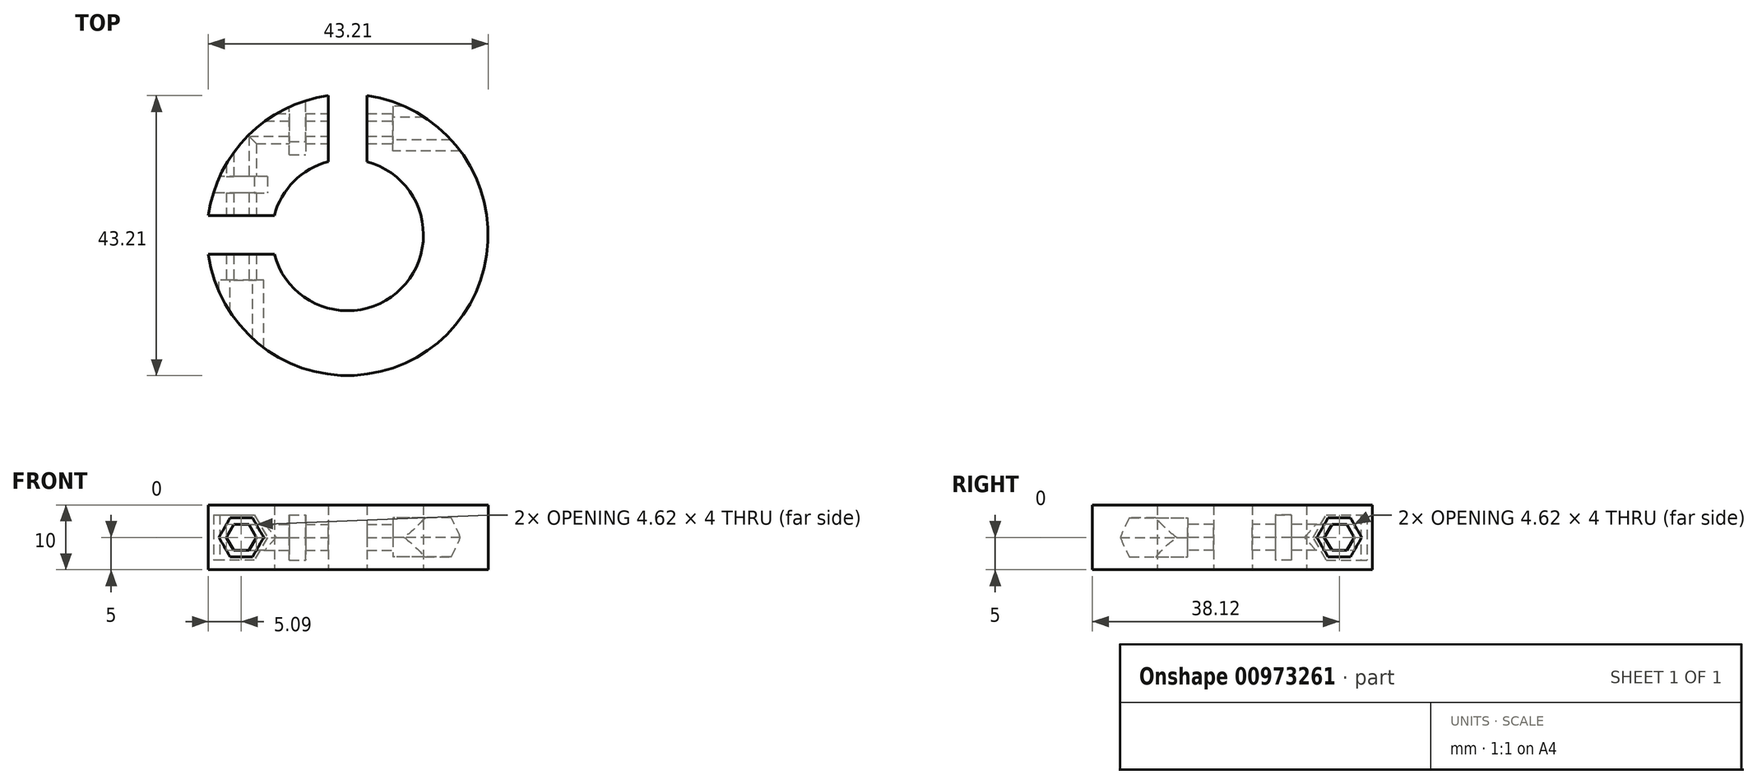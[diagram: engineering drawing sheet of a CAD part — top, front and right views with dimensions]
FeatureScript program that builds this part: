
annotation { "Feature Type Name" : "Feature", "Feature Type Description" : "" }
export const myFeature = defineFeature(function(context is Context, id is Id, definition is map)
    precondition{}
    {
        {
            var Q0;
            Q0=qCreatedBy(makeId("Top.planeOp"),FACE);
            var sketch = newSketch(context, id + "F0", { "sketchPlane" : qUnion([Q0])});
            skCircle(sketch, "E0", {"center": v(0, 0) * mm, "radius": 11.71 * mm});
            skCircle(sketch, "E1", {"center": v(0, 0) * mm, "radius": 21.71 * mm});
            skLineSegment(sketch, "E2.bottom", {"start": v(3, 6.36) * mm, "end": v(-3, 6.36) * mm});
            skLineSegment(sketch, "E2.top", {"start": v(3, 26.36) * mm, "end": v(-3, 26.36) * mm});
            skLineSegment(sketch, "E2.left", {"start": v(3, 6.36) * mm, "end": v(3, 26.36) * mm});
            skLineSegment(sketch, "E2.right", {"start": v(-3, 6.36) * mm, "end": v(-3, 26.36) * mm});
            skPoint(sketch, "E2.middle", {"position": v(0, 16.36) * mm});
            skLineSegment(sketch, "E3.bottom", {"start": v(-26.5, 3) * mm, "end": v(-6.5, 3) * mm});
            skLineSegment(sketch, "E3.top", {"start": v(-26.5, -3) * mm, "end": v(-6.5, -3) * mm});
            skLineSegment(sketch, "E3.left", {"start": v(-26.5, 3) * mm, "end": v(-26.5, -3) * mm});
            skLineSegment(sketch, "E3.right", {"start": v(-6.5, 3) * mm, "end": v(-6.5, -3) * mm});
            skPoint(sketch, "E3.middle", {"position": v(-16.5, 0) * mm});
            skSolve(sketch);
        }
        {
            var Q0;
            {var subQ0=sQuery(id+"F0.wireOp",EDGE,"E2.right");var subQ1=sQuery(id+"F0.wireOp",EDGE,"E0");var subQ2=makeQuery(id+"F0.imprint","INTERSECT",VERTEX,{"derivedFrom":[subQ1,subQ0]});Q0=makeQuery(id+"F0.imprint","IMPRINT",FACE,{"disambiguationData":[TD([[makeQuery(id+"F0.imprint","IMPRINT",EDGE,{"disambiguationData":[TD([[subQ2,-1.0]])],"derivedFrom":subQ1}),-1.0]])]});}
            var Q1;
            {var subQ0=sQuery(id+"F0.wireOp",EDGE,"E2.left");var subQ1=sQuery(id+"F0.wireOp",EDGE,"E0");var subQ2=makeQuery(id+"F0.imprint","INTERSECT",VERTEX,{"derivedFrom":[subQ1,subQ0]});Q1=makeQuery(id+"F0.imprint","IMPRINT",FACE,{"disambiguationData":[TD([[makeQuery(id+"F0.imprint","IMPRINT",EDGE,{"disambiguationData":[TD([[subQ2,1.0]])],"derivedFrom":subQ1}),-1.0]])]});}
            extrude(context, id + "F1", {"entities" : qUnion([Q0, Q1]), "depth" : 10 * mm, "offsetDistance" : 25 * mm});
        }
        {
            var Q0;
            Q0=makeQuery(id+"F1.opExtrude","SWEPT_FACE",FACE,{"disambiguationData":[OSD([sQuery(id+"F0.wireOp",EDGE,"E3.bottom")])]});
            var sketch = newSketch(context, id + "F2", { "sketchPlane" : qUnion([Q0])});
            skCircle(sketch, "E4", {"center": v(-16.41, 5) * mm, "radius": 2 * mm});
            skPoint(sketch, "E4.centerSnap0", {"position": v(-11.32, 5) * mm});
            skPoint(sketch, "E4.centerSnap1", {"position": v(-16.41, 10) * mm});
            skCircle(sketch, "E5", {"center": v(-16.41, 5) * mm, "radius": 3 * mm});
            skCircle(sketch, "E6.cCircle", {"center": v(-16.41, 5) * mm, "radius": 2 * mm, "construction": true});
            skLineSegment(sketch, "E6.0", {"start": v(-15.26, 3) * mm, "end": v(-17.57, 3) * mm});
            skLineSegment(sketch, "E6.1", {"start": v(-17.57, 3) * mm, "end": v(-18.72, 5) * mm});
            skLineSegment(sketch, "E6.2", {"start": v(-18.72, 5) * mm, "end": v(-17.57, 7) * mm});
            skLineSegment(sketch, "E6.3", {"start": v(-17.57, 7) * mm, "end": v(-15.26, 7) * mm});
            skLineSegment(sketch, "E6.4", {"start": v(-15.26, 7) * mm, "end": v(-14.1, 5) * mm});
            skLineSegment(sketch, "E6.5", {"start": v(-14.1, 5) * mm, "end": v(-15.26, 3) * mm});
            skPoint(sketch, "E6.0.midPoint", {"position": v(-16.41, 3) * mm});
            skCircle(sketch, "E7.cCircle", {"center": v(-16.41, 5) * mm, "radius": 3 * mm, "construction": true});
            skLineSegment(sketch, "E7.0", {"start": v(-14.68, 2) * mm, "end": v(-18.14, 2) * mm});
            skLineSegment(sketch, "E7.1", {"start": v(-18.14, 2) * mm, "end": v(-19.87, 5) * mm});
            skLineSegment(sketch, "E7.2", {"start": v(-19.87, 5) * mm, "end": v(-18.14, 8) * mm});
            skLineSegment(sketch, "E7.3", {"start": v(-18.14, 8) * mm, "end": v(-14.68, 8) * mm});
            skLineSegment(sketch, "E7.4", {"start": v(-14.68, 8) * mm, "end": v(-12.95, 5) * mm});
            skLineSegment(sketch, "E7.5", {"start": v(-12.95, 5) * mm, "end": v(-14.68, 2) * mm});
            skPoint(sketch, "E7.0.midPoint", {"position": v(-16.41, 2) * mm});
            skCircle(sketch, "E8.cCircle", {"center": v(-16.41, 5) * mm, "radius": 3.5 * mm, "construction": true});
            skLineSegment(sketch, "E8.0", {"start": v(-18.43, 8.5) * mm, "end": v(-14.39, 8.5) * mm});
            skLineSegment(sketch, "E8.1", {"start": v(-14.39, 8.5) * mm, "end": v(-12.37, 5) * mm});
            skLineSegment(sketch, "E8.2", {"start": v(-12.37, 5) * mm, "end": v(-14.39, 1.5) * mm});
            skLineSegment(sketch, "E8.3", {"start": v(-14.39, 1.5) * mm, "end": v(-18.43, 1.5) * mm});
            skLineSegment(sketch, "E8.4", {"start": v(-18.43, 1.5) * mm, "end": v(-20.45, 5) * mm});
            skLineSegment(sketch, "E8.5", {"start": v(-20.45, 5) * mm, "end": v(-18.43, 8.5) * mm});
            skPoint(sketch, "E8.0.midPoint", {"position": v(-16.41, 8.5) * mm});
            skLineSegment(sketch, "E9", {"start": v(-18.43, 1.5) * mm, "end": v(-21.5, 1.5) * mm});
            skLineSegment(sketch, "E10", {"start": v(-21.5, 1.5) * mm, "end": v(-21.5, 8.5) * mm});
            skLineSegment(sketch, "E11", {"start": v(-21.5, 8.5) * mm, "end": v(-18.43, 8.5) * mm});
            skSolve(sketch);
        }
        {
            var Q0;
            {var subQ0=sQuery(id+"F2.wireOp",EDGE,"E6.1");var subQ1=sQuery(id+"F2.wireOp",EDGE,"E4");var subQ2=makeQuery(id+"F2.imprint","INTERSECT",VERTEX,{"derivedFrom":[subQ1,subQ0]});Q0=makeQuery(id+"F2.imprint","IMPRINT",FACE,{"disambiguationData":[TD([[makeQuery(id+"F2.imprint","IMPRINT",EDGE,{"disambiguationData":[TD([[subQ2,-1.0]])],"derivedFrom":subQ1}),-1.0]])]});}
            var Q1;
            {var subQ0=sQuery(id+"F2.wireOp",EDGE,"E6.0");var subQ1=sQuery(id+"F2.wireOp",EDGE,"E4");var subQ2=makeQuery(id+"F2.imprint","INTERSECT",VERTEX,{"derivedFrom":[subQ1,subQ0]});Q1=makeQuery(id+"F2.imprint","IMPRINT",FACE,{"disambiguationData":[TD([[makeQuery(id+"F2.imprint","IMPRINT",EDGE,{"disambiguationData":[TD([[subQ2,-1.0]])],"derivedFrom":subQ1}),-1.0]])]});}
            var Q2;
            {var subQ0=sQuery(id+"F2.wireOp",EDGE,"E6.4");var subQ1=sQuery(id+"F2.wireOp",EDGE,"E4");var subQ2=makeQuery(id+"F2.imprint","INTERSECT",VERTEX,{"derivedFrom":[subQ1,subQ0]});Q2=makeQuery(id+"F2.imprint","IMPRINT",FACE,{"disambiguationData":[TD([[makeQuery(id+"F2.imprint","IMPRINT",EDGE,{"disambiguationData":[TD([[subQ2,1.0]])],"derivedFrom":subQ1}),-1.0]])]});}
            var Q3;
            {var subQ0=sQuery(id+"F2.wireOp",EDGE,"E6.3");var subQ1=sQuery(id+"F2.wireOp",EDGE,"E4");var subQ2=makeQuery(id+"F2.imprint","INTERSECT",VERTEX,{"derivedFrom":[subQ1,subQ0]});Q3=makeQuery(id+"F2.imprint","IMPRINT",FACE,{"disambiguationData":[TD([[makeQuery(id+"F2.imprint","IMPRINT",EDGE,{"disambiguationData":[TD([[subQ2,1.0]])],"derivedFrom":subQ1}),-1.0]])]});}
            var Q4;
            {var subQ0=sQuery(id+"F2.wireOp",EDGE,"E6.2");var subQ1=sQuery(id+"F2.wireOp",EDGE,"E4");var subQ2=makeQuery(id+"F2.imprint","INTERSECT",VERTEX,{"derivedFrom":[subQ1,subQ0]});Q4=makeQuery(id+"F2.imprint","IMPRINT",FACE,{"disambiguationData":[TD([[makeQuery(id+"F2.imprint","IMPRINT",EDGE,{"disambiguationData":[TD([[subQ2,-1.0]])],"derivedFrom":subQ1}),-1.0]])]});}
            var Q5;
            {var subQ0=sQuery(id+"F2.wireOp",EDGE,"E4");var subQ4=makeQuery(id+"F2.imprint","INTERSECT",VERTEX,{"derivedFrom":[subQ0,sQuery(id+"F2.wireOp",EDGE,"E6.3")]});Q5=makeQuery(id+"F2.imprint","IMPRINT",FACE,{"disambiguationData":[TD([[makeQuery(id+"F2.imprint","IMPRINT",EDGE,{"disambiguationData":[TD([[subQ4,1.0]])],"derivedFrom":subQ0}),1.0]])]});}
            var Q6;
            {var subQ0=sQuery(id+"F2.wireOp",EDGE,"E6.3");var subQ1=sQuery(id+"F2.wireOp",EDGE,"E4");var subQ2=makeQuery(id+"F2.imprint","INTERSECT",VERTEX,{"derivedFrom":[subQ1,subQ0]});Q6=makeQuery(id+"F2.imprint","IMPRINT",FACE,{"disambiguationData":[TD([[makeQuery(id+"F2.imprint","IMPRINT",EDGE,{"disambiguationData":[TD([[subQ2,-1.0]])],"derivedFrom":subQ1}),-1.0]])]});}
            extrude(context, id + "F3", {"entities" : qUnion([Q0, Q1, Q2, Q3, Q4, Q5, Q6]), "operationType" : NewBodyOperationType.REMOVE, "endBound" : BoundingType.THROUGH_ALL, "oppositeDirection" : true, "depth" : 25 * mm, "offsetDistance" : 25 * mm, "hasSecondDirection" : true, "secondDirectionBound" : SecondDirectionBoundingType.THROUGH_ALL, "secondDirectionOppositeDirection" : false, "secondDirectionDepth" : 25 * mm});
        }
        {
            var Q0;
            Q0=makeQuery(id+"F1.opExtrude","SWEPT_FACE",FACE,{"disambiguationData":[OSD([sQuery(id+"F0.wireOp",EDGE,"E2.right")])]});
            var sketch = newSketch(context, id + "F4", { "sketchPlane" : qUnion([Q0])});
            skCircle(sketch, "E12", {"center": v(16.41, 5) * mm, "radius": 2 * mm});
            skPoint(sketch, "E12.centerSnap0", {"position": v(21.5, 5) * mm});
            skPoint(sketch, "E12.centerSnap1", {"position": v(16.41, 10) * mm});
            skCircle(sketch, "E13", {"center": v(16.41, 5) * mm, "radius": 3 * mm});
            skCircle(sketch, "E14.cCircle", {"center": v(16.41, 5) * mm, "radius": 2 * mm, "construction": true});
            skLineSegment(sketch, "E14.0", {"start": v(17.57, 3) * mm, "end": v(15.26, 3) * mm});
            skLineSegment(sketch, "E14.1", {"start": v(15.26, 3) * mm, "end": v(14.1, 5) * mm});
            skLineSegment(sketch, "E14.2", {"start": v(14.1, 5) * mm, "end": v(15.26, 7) * mm});
            skLineSegment(sketch, "E14.3", {"start": v(15.26, 7) * mm, "end": v(17.57, 7) * mm});
            skLineSegment(sketch, "E14.4", {"start": v(17.57, 7) * mm, "end": v(18.72, 5) * mm});
            skLineSegment(sketch, "E14.5", {"start": v(18.72, 5) * mm, "end": v(17.57, 3) * mm});
            skPoint(sketch, "E14.0.midPoint", {"position": v(16.41, 3) * mm});
            skCircle(sketch, "E15.cCircle", {"center": v(16.41, 5) * mm, "radius": 3 * mm, "construction": true});
            skLineSegment(sketch, "E15.0", {"start": v(18.14, 2) * mm, "end": v(14.68, 2) * mm});
            skLineSegment(sketch, "E15.1", {"start": v(14.68, 2) * mm, "end": v(12.95, 5) * mm});
            skLineSegment(sketch, "E15.2", {"start": v(12.95, 5) * mm, "end": v(14.68, 8) * mm});
            skLineSegment(sketch, "E15.3", {"start": v(14.68, 8) * mm, "end": v(18.14, 8) * mm});
            skLineSegment(sketch, "E15.4", {"start": v(18.14, 8) * mm, "end": v(19.87, 5) * mm});
            skLineSegment(sketch, "E15.5", {"start": v(19.87, 5) * mm, "end": v(18.14, 2) * mm});
            skPoint(sketch, "E15.0.midPoint", {"position": v(16.41, 2) * mm});
            skCircle(sketch, "E16.cCircle", {"center": v(16.41, 5) * mm, "radius": 3.5 * mm, "construction": true});
            skLineSegment(sketch, "E16.0", {"start": v(18.43, 1.5) * mm, "end": v(14.39, 1.5) * mm});
            skLineSegment(sketch, "E16.1", {"start": v(14.39, 1.5) * mm, "end": v(12.37, 5) * mm});
            skLineSegment(sketch, "E16.2", {"start": v(12.37, 5) * mm, "end": v(14.39, 8.5) * mm});
            skLineSegment(sketch, "E16.3", {"start": v(14.39, 8.5) * mm, "end": v(18.43, 8.5) * mm});
            skLineSegment(sketch, "E16.4", {"start": v(18.43, 8.5) * mm, "end": v(20.45, 5) * mm});
            skLineSegment(sketch, "E16.5", {"start": v(20.45, 5) * mm, "end": v(18.43, 1.5) * mm});
            skPoint(sketch, "E16.0.midPoint", {"position": v(16.41, 1.5) * mm});
            skLineSegment(sketch, "E17", {"start": v(18.43, 8.5) * mm, "end": v(21.5, 8.5) * mm});
            skLineSegment(sketch, "E18", {"start": v(18.43, 1.5) * mm, "end": v(21.5, 1.5) * mm});
            skLineSegment(sketch, "E19", {"start": v(21.5, 1.5) * mm, "end": v(21.5, 8.5) * mm});
            skLineSegment(sketch, "E20", {"start": v(21.5, 8.5) * mm, "end": v(18.43, 8.5) * mm});
            skSolve(sketch);
        }
        {
            var Q0;
            {var subQ0=sQuery(id+"F4.wireOp",EDGE,"E14.3");var subQ1=sQuery(id+"F4.wireOp",EDGE,"E12");var subQ2=makeQuery(id+"F4.imprint","INTERSECT",VERTEX,{"derivedFrom":[subQ1,subQ0]});Q0=makeQuery(id+"F4.imprint","IMPRINT",FACE,{"disambiguationData":[TD([[makeQuery(id+"F4.imprint","IMPRINT",EDGE,{"disambiguationData":[TD([[subQ2,1.0]])],"derivedFrom":subQ1}),-1.0]])]});}
            var Q1;
            {var subQ0=sQuery(id+"F4.wireOp",EDGE,"E14.0");var subQ1=sQuery(id+"F4.wireOp",EDGE,"E12");var subQ2=makeQuery(id+"F4.imprint","INTERSECT",VERTEX,{"derivedFrom":[subQ1,subQ0]});Q1=makeQuery(id+"F4.imprint","IMPRINT",FACE,{"disambiguationData":[TD([[makeQuery(id+"F4.imprint","IMPRINT",EDGE,{"disambiguationData":[TD([[subQ2,-1.0]])],"derivedFrom":subQ1}),-1.0]])]});}
            var Q2;
            {var subQ0=sQuery(id+"F4.wireOp",EDGE,"E14.4");var subQ1=sQuery(id+"F4.wireOp",EDGE,"E12");var subQ2=makeQuery(id+"F4.imprint","INTERSECT",VERTEX,{"derivedFrom":[subQ1,subQ0]});Q2=makeQuery(id+"F4.imprint","IMPRINT",FACE,{"disambiguationData":[TD([[makeQuery(id+"F4.imprint","IMPRINT",EDGE,{"disambiguationData":[TD([[subQ2,1.0]])],"derivedFrom":subQ1}),-1.0]])]});}
            var Q3;
            {var subQ0=sQuery(id+"F4.wireOp",EDGE,"E14.3");var subQ1=sQuery(id+"F4.wireOp",EDGE,"E12");var subQ2=makeQuery(id+"F4.imprint","INTERSECT",VERTEX,{"derivedFrom":[subQ1,subQ0]});Q3=makeQuery(id+"F4.imprint","IMPRINT",FACE,{"disambiguationData":[TD([[makeQuery(id+"F4.imprint","IMPRINT",EDGE,{"disambiguationData":[TD([[subQ2,-1.0]])],"derivedFrom":subQ1}),-1.0]])]});}
            var Q4;
            {var subQ0=sQuery(id+"F4.wireOp",EDGE,"E14.2");var subQ1=sQuery(id+"F4.wireOp",EDGE,"E12");var subQ2=makeQuery(id+"F4.imprint","INTERSECT",VERTEX,{"derivedFrom":[subQ1,subQ0]});Q4=makeQuery(id+"F4.imprint","IMPRINT",FACE,{"disambiguationData":[TD([[makeQuery(id+"F4.imprint","IMPRINT",EDGE,{"disambiguationData":[TD([[subQ2,-1.0]])],"derivedFrom":subQ1}),-1.0]])]});}
            var Q5;
            {var subQ0=sQuery(id+"F4.wireOp",EDGE,"E14.1");var subQ1=sQuery(id+"F4.wireOp",EDGE,"E12");var subQ2=makeQuery(id+"F4.imprint","INTERSECT",VERTEX,{"derivedFrom":[subQ1,subQ0]});Q5=makeQuery(id+"F4.imprint","IMPRINT",FACE,{"disambiguationData":[TD([[makeQuery(id+"F4.imprint","IMPRINT",EDGE,{"disambiguationData":[TD([[subQ2,-1.0]])],"derivedFrom":subQ1}),-1.0]])]});}
            var Q6;
            {var subQ0=sQuery(id+"F4.wireOp",EDGE,"E12");var subQ4=makeQuery(id+"F4.imprint","INTERSECT",VERTEX,{"derivedFrom":[subQ0,sQuery(id+"F4.wireOp",EDGE,"E14.3")]});Q6=makeQuery(id+"F4.imprint","IMPRINT",FACE,{"disambiguationData":[TD([[makeQuery(id+"F4.imprint","IMPRINT",EDGE,{"disambiguationData":[TD([[subQ4,1.0]])],"derivedFrom":subQ0}),1.0]])]});}
            extrude(context, id + "F5", {"entities" : qUnion([Q0, Q1, Q2, Q3, Q4, Q5, Q6]), "operationType" : NewBodyOperationType.REMOVE, "endBound" : BoundingType.THROUGH_ALL, "oppositeDirection" : true, "depth" : 25 * mm, "offsetDistance" : 25 * mm, "hasSecondDirection" : true, "secondDirectionBound" : SecondDirectionBoundingType.THROUGH_ALL, "secondDirectionOppositeDirection" : false, "secondDirectionDepth" : 25 * mm});
        }
        {
            var Q0;
            Q0=makeQuery(id+"F2.imprint","IMPRINT",FACE,{"disambiguationData":[TD([[makeQuery(id+"F2.imprint","IMPRINT",EDGE,{"derivedFrom":sQuery(id+"F2.wireOp",EDGE,"E4")}),-1.0]])]});
            var Q1;
            {var subQ10=sQuery(id+"F2.wireOp",EDGE,"E5");var subQ14=makeQuery(id+"F2.imprint","INTERSECT",VERTEX,{"derivedFrom":[subQ10,sQuery(id+"F2.wireOp",EDGE,"E7.3")]});Q1=makeQuery(id+"F2.imprint","IMPRINT",FACE,{"disambiguationData":[TD([[makeQuery(id+"F2.imprint","IMPRINT",EDGE,{"disambiguationData":[TD([[subQ14,1.0]])],"derivedFrom":subQ10}),1.0]])]});}
            var Q2;
            {var subQ0=sQuery(id+"F2.wireOp",EDGE,"E7.3");var subQ1=sQuery(id+"F2.wireOp",EDGE,"E5");var subQ2=makeQuery(id+"F2.imprint","INTERSECT",VERTEX,{"derivedFrom":[subQ1,subQ0]});Q2=makeQuery(id+"F2.imprint","IMPRINT",FACE,{"disambiguationData":[TD([[makeQuery(id+"F2.imprint","IMPRINT",EDGE,{"disambiguationData":[TD([[subQ2,-1.0]])],"derivedFrom":subQ1}),-1.0]])]});}
            var Q3;
            {var subQ0=sQuery(id+"F2.wireOp",EDGE,"E7.2");var subQ1=sQuery(id+"F2.wireOp",EDGE,"E5");var subQ2=makeQuery(id+"F2.imprint","INTERSECT",VERTEX,{"derivedFrom":[subQ1,subQ0]});Q3=makeQuery(id+"F2.imprint","IMPRINT",FACE,{"disambiguationData":[TD([[makeQuery(id+"F2.imprint","IMPRINT",EDGE,{"disambiguationData":[TD([[subQ2,-1.0]])],"derivedFrom":subQ1}),-1.0]])]});}
            var Q4;
            {var subQ0=sQuery(id+"F2.wireOp",EDGE,"E7.1");var subQ1=sQuery(id+"F2.wireOp",EDGE,"E5");var subQ2=makeQuery(id+"F2.imprint","INTERSECT",VERTEX,{"derivedFrom":[subQ1,subQ0]});Q4=makeQuery(id+"F2.imprint","IMPRINT",FACE,{"disambiguationData":[TD([[makeQuery(id+"F2.imprint","IMPRINT",EDGE,{"disambiguationData":[TD([[subQ2,-1.0]])],"derivedFrom":subQ1}),-1.0]])]});}
            var Q5;
            {var subQ0=sQuery(id+"F2.wireOp",EDGE,"E7.0");var subQ1=sQuery(id+"F2.wireOp",EDGE,"E5");var subQ2=makeQuery(id+"F2.imprint","INTERSECT",VERTEX,{"derivedFrom":[subQ1,subQ0]});Q5=makeQuery(id+"F2.imprint","IMPRINT",FACE,{"disambiguationData":[TD([[makeQuery(id+"F2.imprint","IMPRINT",EDGE,{"disambiguationData":[TD([[subQ2,-1.0]])],"derivedFrom":subQ1}),-1.0]])]});}
            var Q6;
            {var subQ0=sQuery(id+"F2.wireOp",EDGE,"E7.4");var subQ1=sQuery(id+"F2.wireOp",EDGE,"E5");var subQ2=makeQuery(id+"F2.imprint","INTERSECT",VERTEX,{"derivedFrom":[subQ1,subQ0]});Q6=makeQuery(id+"F2.imprint","IMPRINT",FACE,{"disambiguationData":[TD([[makeQuery(id+"F2.imprint","IMPRINT",EDGE,{"disambiguationData":[TD([[subQ2,1.0]])],"derivedFrom":subQ1}),-1.0]])]});}
            var Q7;
            {var subQ0=sQuery(id+"F2.wireOp",EDGE,"E7.3");var subQ1=sQuery(id+"F2.wireOp",EDGE,"E5");var subQ2=makeQuery(id+"F2.imprint","INTERSECT",VERTEX,{"derivedFrom":[subQ1,subQ0]});Q7=makeQuery(id+"F2.imprint","IMPRINT",FACE,{"disambiguationData":[TD([[makeQuery(id+"F2.imprint","IMPRINT",EDGE,{"disambiguationData":[TD([[subQ2,1.0]])],"derivedFrom":subQ1}),-1.0]])]});}
            extrude(context, id + "F6", {"entities" : qUnion([Q0, Q1, Q2, Q3, Q4, Q5, Q6, Q7]), "operationType" : NewBodyOperationType.REMOVE, "depth" : 25 * mm, "offsetDistance" : 25 * mm, "hasSecondDirection" : true, "secondDirectionOppositeDirection" : false, "secondDirectionDepth" : 10 * mm});
        }
        {
            var Q0;
            Q0=makeQuery(id+"F4.imprint","IMPRINT",FACE,{"disambiguationData":[TD([[makeQuery(id+"F4.imprint","IMPRINT",EDGE,{"derivedFrom":sQuery(id+"F4.wireOp",EDGE,"E12")}),-1.0]])]});
            var Q1;
            {var subQ0=sQuery(id+"F4.wireOp",EDGE,"E15.0");var subQ1=sQuery(id+"F4.wireOp",EDGE,"E13");var subQ2=makeQuery(id+"F4.imprint","INTERSECT",VERTEX,{"derivedFrom":[subQ1,subQ0]});Q1=makeQuery(id+"F4.imprint","IMPRINT",FACE,{"disambiguationData":[TD([[makeQuery(id+"F4.imprint","IMPRINT",EDGE,{"disambiguationData":[TD([[subQ2,-1.0]])],"derivedFrom":subQ1}),-1.0]])]});}
            var Q2;
            {var subQ0=sQuery(id+"F4.wireOp",EDGE,"E15.1");var subQ1=sQuery(id+"F4.wireOp",EDGE,"E13");var subQ2=makeQuery(id+"F4.imprint","INTERSECT",VERTEX,{"derivedFrom":[subQ1,subQ0]});Q2=makeQuery(id+"F4.imprint","IMPRINT",FACE,{"disambiguationData":[TD([[makeQuery(id+"F4.imprint","IMPRINT",EDGE,{"disambiguationData":[TD([[subQ2,-1.0]])],"derivedFrom":subQ1}),-1.0]])]});}
            var Q3;
            {var subQ0=sQuery(id+"F4.wireOp",EDGE,"E15.2");var subQ1=sQuery(id+"F4.wireOp",EDGE,"E13");var subQ2=makeQuery(id+"F4.imprint","INTERSECT",VERTEX,{"derivedFrom":[subQ1,subQ0]});Q3=makeQuery(id+"F4.imprint","IMPRINT",FACE,{"disambiguationData":[TD([[makeQuery(id+"F4.imprint","IMPRINT",EDGE,{"disambiguationData":[TD([[subQ2,-1.0]])],"derivedFrom":subQ1}),-1.0]])]});}
            var Q4;
            {var subQ0=sQuery(id+"F4.wireOp",EDGE,"E15.3");var subQ1=sQuery(id+"F4.wireOp",EDGE,"E13");var subQ2=makeQuery(id+"F4.imprint","INTERSECT",VERTEX,{"derivedFrom":[subQ1,subQ0]});Q4=makeQuery(id+"F4.imprint","IMPRINT",FACE,{"disambiguationData":[TD([[makeQuery(id+"F4.imprint","IMPRINT",EDGE,{"disambiguationData":[TD([[subQ2,-1.0]])],"derivedFrom":subQ1}),-1.0]])]});}
            var Q5;
            {var subQ0=sQuery(id+"F4.wireOp",EDGE,"E15.3");var subQ1=sQuery(id+"F4.wireOp",EDGE,"E13");var subQ2=makeQuery(id+"F4.imprint","INTERSECT",VERTEX,{"derivedFrom":[subQ1,subQ0]});Q5=makeQuery(id+"F4.imprint","IMPRINT",FACE,{"disambiguationData":[TD([[makeQuery(id+"F4.imprint","IMPRINT",EDGE,{"disambiguationData":[TD([[subQ2,1.0]])],"derivedFrom":subQ1}),-1.0]])]});}
            var Q6;
            {var subQ0=sQuery(id+"F4.wireOp",EDGE,"E15.4");var subQ1=sQuery(id+"F4.wireOp",EDGE,"E13");var subQ2=makeQuery(id+"F4.imprint","INTERSECT",VERTEX,{"derivedFrom":[subQ1,subQ0]});Q6=makeQuery(id+"F4.imprint","IMPRINT",FACE,{"disambiguationData":[TD([[makeQuery(id+"F4.imprint","IMPRINT",EDGE,{"disambiguationData":[TD([[subQ2,1.0]])],"derivedFrom":subQ1}),-1.0]])]});}
            var Q7;
            {var subQ10=sQuery(id+"F4.wireOp",EDGE,"E13");var subQ14=makeQuery(id+"F4.imprint","INTERSECT",VERTEX,{"derivedFrom":[subQ10,sQuery(id+"F4.wireOp",EDGE,"E15.3")]});Q7=makeQuery(id+"F4.imprint","IMPRINT",FACE,{"disambiguationData":[TD([[makeQuery(id+"F4.imprint","IMPRINT",EDGE,{"disambiguationData":[TD([[subQ14,1.0]])],"derivedFrom":subQ10}),1.0]])]});}
            extrude(context, id + "F7", {"entities" : qUnion([Q0, Q1, Q2, Q3, Q4, Q5, Q6, Q7]), "operationType" : NewBodyOperationType.REMOVE, "depth" : 25 * mm, "offsetDistance" : 25 * mm, "hasSecondDirection" : true, "secondDirectionOppositeDirection" : false, "secondDirectionDepth" : 10 * mm});
        }
        {
            var Q0;
            Q0=makeQuery(id+"F1.opExtrude","SWEPT_FACE",FACE,{"disambiguationData":[OSD([sQuery(id+"F0.wireOp",EDGE,"E2.left")])]});
            var sketch = newSketch(context, id + "F8", { "sketchPlane" : qUnion([Q0])});
            skCircle(sketch, "E21", {"center": v(-16.41, 5) * mm, "radius": 1.5 * mm});
            skPoint(sketch, "E21.centerSnap0", {"position": v(-16.41, 10) * mm});
            skPoint(sketch, "E21.centerSnap1", {"position": v(-11.32, 5) * mm});
            skSolve(sketch);
        }
        {
            var Q0;
            Q0=makeQuery(id+"F8.imprint","IMPRINT",FACE,{"disambiguationData":[TD([[makeQuery(id+"F8.imprint","IMPRINT",EDGE,{"derivedFrom":sQuery(id+"F8.wireOp",EDGE,"E21")}),1.0]])]});
            extrude(context, id + "F9", {"entities" : qUnion([Q0]), "operationType" : NewBodyOperationType.REMOVE, "oppositeDirection" : true, "depth" : 25 * mm, "offsetDistance" : 25 * mm});
        }
        {
            var Q0;
            Q0=makeQuery(id+"F1.opExtrude","SWEPT_FACE",FACE,{"disambiguationData":[OSD([sQuery(id+"F0.wireOp",EDGE,"E3.top")])]});
            var sketch = newSketch(context, id + "F10", { "sketchPlane" : qUnion([Q0])});
            skCircle(sketch, "E22", {"center": v(16.41, 5) * mm, "radius": 1.5 * mm});
            skPoint(sketch, "E22.centerSnap0", {"position": v(16.41, 10) * mm});
            skPoint(sketch, "E22.centerSnap1", {"position": v(21.5, 5) * mm});
            skSolve(sketch);
        }
        {
            var Q0;
            Q0=makeQuery(id+"F10.imprint","IMPRINT",FACE,{"disambiguationData":[TD([[makeQuery(id+"F10.imprint","IMPRINT",EDGE,{"derivedFrom":sQuery(id+"F10.wireOp",EDGE,"E22")}),1.0]])]});
            extrude(context, id + "F11", {"entities" : qUnion([Q0]), "operationType" : NewBodyOperationType.REMOVE, "oppositeDirection" : true, "depth" : 25 * mm, "offsetDistance" : 25 * mm});
        }
        {
            var Q0;
            Q0=makeQuery(id+"F4.imprint","IMPRINT",FACE,{"disambiguationData":[TD([[makeQuery(id+"F4.imprint","IMPRINT",EDGE,{"derivedFrom":sQuery(id+"F4.wireOp",EDGE,"E16.4")}),1.0]])]});
            var Q1;
            Q1=makeQuery(id+"F4.imprint","IMPRINT",FACE,{"disambiguationData":[TD([[makeQuery(id+"F4.imprint","IMPRINT",EDGE,{"derivedFrom":sQuery(id+"F4.wireOp",EDGE,"E16.0")}),-1.0]])]});
            var Q2;
            {var subQ0=sQuery(id+"F4.wireOp",EDGE,"E15.4");var subQ1=sQuery(id+"F4.wireOp",EDGE,"E13");var subQ2=makeQuery(id+"F4.imprint","INTERSECT",VERTEX,{"derivedFrom":[subQ1,subQ0]});Q2=makeQuery(id+"F4.imprint","IMPRINT",FACE,{"disambiguationData":[TD([[makeQuery(id+"F4.imprint","IMPRINT",EDGE,{"disambiguationData":[TD([[subQ2,1.0]])],"derivedFrom":subQ1}),-1.0]])]});}
            var Q3;
            {var subQ0=sQuery(id+"F4.wireOp",EDGE,"E15.3");var subQ1=sQuery(id+"F4.wireOp",EDGE,"E13");var subQ2=makeQuery(id+"F4.imprint","INTERSECT",VERTEX,{"derivedFrom":[subQ1,subQ0]});Q3=makeQuery(id+"F4.imprint","IMPRINT",FACE,{"disambiguationData":[TD([[makeQuery(id+"F4.imprint","IMPRINT",EDGE,{"disambiguationData":[TD([[subQ2,1.0]])],"derivedFrom":subQ1}),-1.0]])]});}
            var Q4;
            {var subQ0=sQuery(id+"F4.wireOp",EDGE,"E15.0");var subQ1=sQuery(id+"F4.wireOp",EDGE,"E13");var subQ2=makeQuery(id+"F4.imprint","INTERSECT",VERTEX,{"derivedFrom":[subQ1,subQ0]});Q4=makeQuery(id+"F4.imprint","IMPRINT",FACE,{"disambiguationData":[TD([[makeQuery(id+"F4.imprint","IMPRINT",EDGE,{"disambiguationData":[TD([[subQ2,-1.0]])],"derivedFrom":subQ1}),-1.0]])]});}
            var Q5;
            {var subQ0=sQuery(id+"F4.wireOp",EDGE,"E15.1");var subQ1=sQuery(id+"F4.wireOp",EDGE,"E13");var subQ2=makeQuery(id+"F4.imprint","INTERSECT",VERTEX,{"derivedFrom":[subQ1,subQ0]});Q5=makeQuery(id+"F4.imprint","IMPRINT",FACE,{"disambiguationData":[TD([[makeQuery(id+"F4.imprint","IMPRINT",EDGE,{"disambiguationData":[TD([[subQ2,-1.0]])],"derivedFrom":subQ1}),-1.0]])]});}
            var Q6;
            {var subQ0=sQuery(id+"F4.wireOp",EDGE,"E15.2");var subQ1=sQuery(id+"F4.wireOp",EDGE,"E13");var subQ2=makeQuery(id+"F4.imprint","INTERSECT",VERTEX,{"derivedFrom":[subQ1,subQ0]});Q6=makeQuery(id+"F4.imprint","IMPRINT",FACE,{"disambiguationData":[TD([[makeQuery(id+"F4.imprint","IMPRINT",EDGE,{"disambiguationData":[TD([[subQ2,-1.0]])],"derivedFrom":subQ1}),-1.0]])]});}
            var Q7;
            {var subQ0=sQuery(id+"F4.wireOp",EDGE,"E15.3");var subQ1=sQuery(id+"F4.wireOp",EDGE,"E13");var subQ2=makeQuery(id+"F4.imprint","INTERSECT",VERTEX,{"derivedFrom":[subQ1,subQ0]});Q7=makeQuery(id+"F4.imprint","IMPRINT",FACE,{"disambiguationData":[TD([[makeQuery(id+"F4.imprint","IMPRINT",EDGE,{"disambiguationData":[TD([[subQ2,-1.0]])],"derivedFrom":subQ1}),-1.0]])]});}
            var Q8;
            {var subQ10=sQuery(id+"F4.wireOp",EDGE,"E13");var subQ14=makeQuery(id+"F4.imprint","INTERSECT",VERTEX,{"derivedFrom":[subQ10,sQuery(id+"F4.wireOp",EDGE,"E15.3")]});Q8=makeQuery(id+"F4.imprint","IMPRINT",FACE,{"disambiguationData":[TD([[makeQuery(id+"F4.imprint","IMPRINT",EDGE,{"disambiguationData":[TD([[subQ14,1.0]])],"derivedFrom":subQ10}),1.0]])]});}
            extrude(context, id + "F12", {"entities" : qUnion([Q0, Q1, Q2, Q3, Q4, Q5, Q6, Q7, Q8]), "operationType" : NewBodyOperationType.REMOVE, "oppositeDirection" : true, "depth" : 6 * mm, "offsetDistance" : 25 * mm, "hasSecondDirection" : true, "secondDirectionOppositeDirection" : true, "secondDirectionDepth" : 3.5 * mm});
        }
        {
            var Q0;
            Q0=makeQuery(id+"F2.imprint","IMPRINT",FACE,{"disambiguationData":[TD([[makeQuery(id+"F2.imprint","IMPRINT",EDGE,{"derivedFrom":sQuery(id+"F2.wireOp",EDGE,"E8.4")}),1.0]])]});
            var Q1;
            Q1=makeQuery(id+"F2.imprint","IMPRINT",FACE,{"disambiguationData":[TD([[makeQuery(id+"F2.imprint","IMPRINT",EDGE,{"derivedFrom":sQuery(id+"F2.wireOp",EDGE,"E8.0")}),-1.0]])]});
            var Q2;
            {var subQ0=sQuery(id+"F2.wireOp",EDGE,"E7.2");var subQ1=sQuery(id+"F2.wireOp",EDGE,"E5");var subQ2=makeQuery(id+"F2.imprint","INTERSECT",VERTEX,{"derivedFrom":[subQ1,subQ0]});Q2=makeQuery(id+"F2.imprint","IMPRINT",FACE,{"disambiguationData":[TD([[makeQuery(id+"F2.imprint","IMPRINT",EDGE,{"disambiguationData":[TD([[subQ2,-1.0]])],"derivedFrom":subQ1}),-1.0]])]});}
            var Q3;
            {var subQ0=sQuery(id+"F2.wireOp",EDGE,"E7.1");var subQ1=sQuery(id+"F2.wireOp",EDGE,"E5");var subQ2=makeQuery(id+"F2.imprint","INTERSECT",VERTEX,{"derivedFrom":[subQ1,subQ0]});Q3=makeQuery(id+"F2.imprint","IMPRINT",FACE,{"disambiguationData":[TD([[makeQuery(id+"F2.imprint","IMPRINT",EDGE,{"disambiguationData":[TD([[subQ2,-1.0]])],"derivedFrom":subQ1}),-1.0]])]});}
            var Q4;
            {var subQ0=sQuery(id+"F2.wireOp",EDGE,"E7.3");var subQ1=sQuery(id+"F2.wireOp",EDGE,"E5");var subQ2=makeQuery(id+"F2.imprint","INTERSECT",VERTEX,{"derivedFrom":[subQ1,subQ0]});Q4=makeQuery(id+"F2.imprint","IMPRINT",FACE,{"disambiguationData":[TD([[makeQuery(id+"F2.imprint","IMPRINT",EDGE,{"disambiguationData":[TD([[subQ2,-1.0]])],"derivedFrom":subQ1}),-1.0]])]});}
            var Q5;
            {var subQ0=sQuery(id+"F2.wireOp",EDGE,"E7.3");var subQ1=sQuery(id+"F2.wireOp",EDGE,"E5");var subQ2=makeQuery(id+"F2.imprint","INTERSECT",VERTEX,{"derivedFrom":[subQ1,subQ0]});Q5=makeQuery(id+"F2.imprint","IMPRINT",FACE,{"disambiguationData":[TD([[makeQuery(id+"F2.imprint","IMPRINT",EDGE,{"disambiguationData":[TD([[subQ2,1.0]])],"derivedFrom":subQ1}),-1.0]])]});}
            var Q6;
            {var subQ0=sQuery(id+"F2.wireOp",EDGE,"E7.4");var subQ1=sQuery(id+"F2.wireOp",EDGE,"E5");var subQ2=makeQuery(id+"F2.imprint","INTERSECT",VERTEX,{"derivedFrom":[subQ1,subQ0]});Q6=makeQuery(id+"F2.imprint","IMPRINT",FACE,{"disambiguationData":[TD([[makeQuery(id+"F2.imprint","IMPRINT",EDGE,{"disambiguationData":[TD([[subQ2,1.0]])],"derivedFrom":subQ1}),-1.0]])]});}
            var Q7;
            {var subQ0=sQuery(id+"F2.wireOp",EDGE,"E7.0");var subQ1=sQuery(id+"F2.wireOp",EDGE,"E5");var subQ2=makeQuery(id+"F2.imprint","INTERSECT",VERTEX,{"derivedFrom":[subQ1,subQ0]});Q7=makeQuery(id+"F2.imprint","IMPRINT",FACE,{"disambiguationData":[TD([[makeQuery(id+"F2.imprint","IMPRINT",EDGE,{"disambiguationData":[TD([[subQ2,-1.0]])],"derivedFrom":subQ1}),-1.0]])]});}
            var Q8;
            {var subQ10=sQuery(id+"F2.wireOp",EDGE,"E5");var subQ14=makeQuery(id+"F2.imprint","INTERSECT",VERTEX,{"derivedFrom":[subQ10,sQuery(id+"F2.wireOp",EDGE,"E7.3")]});Q8=makeQuery(id+"F2.imprint","IMPRINT",FACE,{"disambiguationData":[TD([[makeQuery(id+"F2.imprint","IMPRINT",EDGE,{"disambiguationData":[TD([[subQ14,1.0]])],"derivedFrom":subQ10}),1.0]])]});}
            extrude(context, id + "F13", {"entities" : qUnion([Q0, Q1, Q2, Q3, Q4, Q5, Q6, Q7, Q8]), "operationType" : NewBodyOperationType.REMOVE, "oppositeDirection" : true, "depth" : 6 * mm, "offsetDistance" : 25 * mm, "hasSecondDirection" : true, "secondDirectionOppositeDirection" : true, "secondDirectionDepth" : 3.5 * mm});
        }
    });
